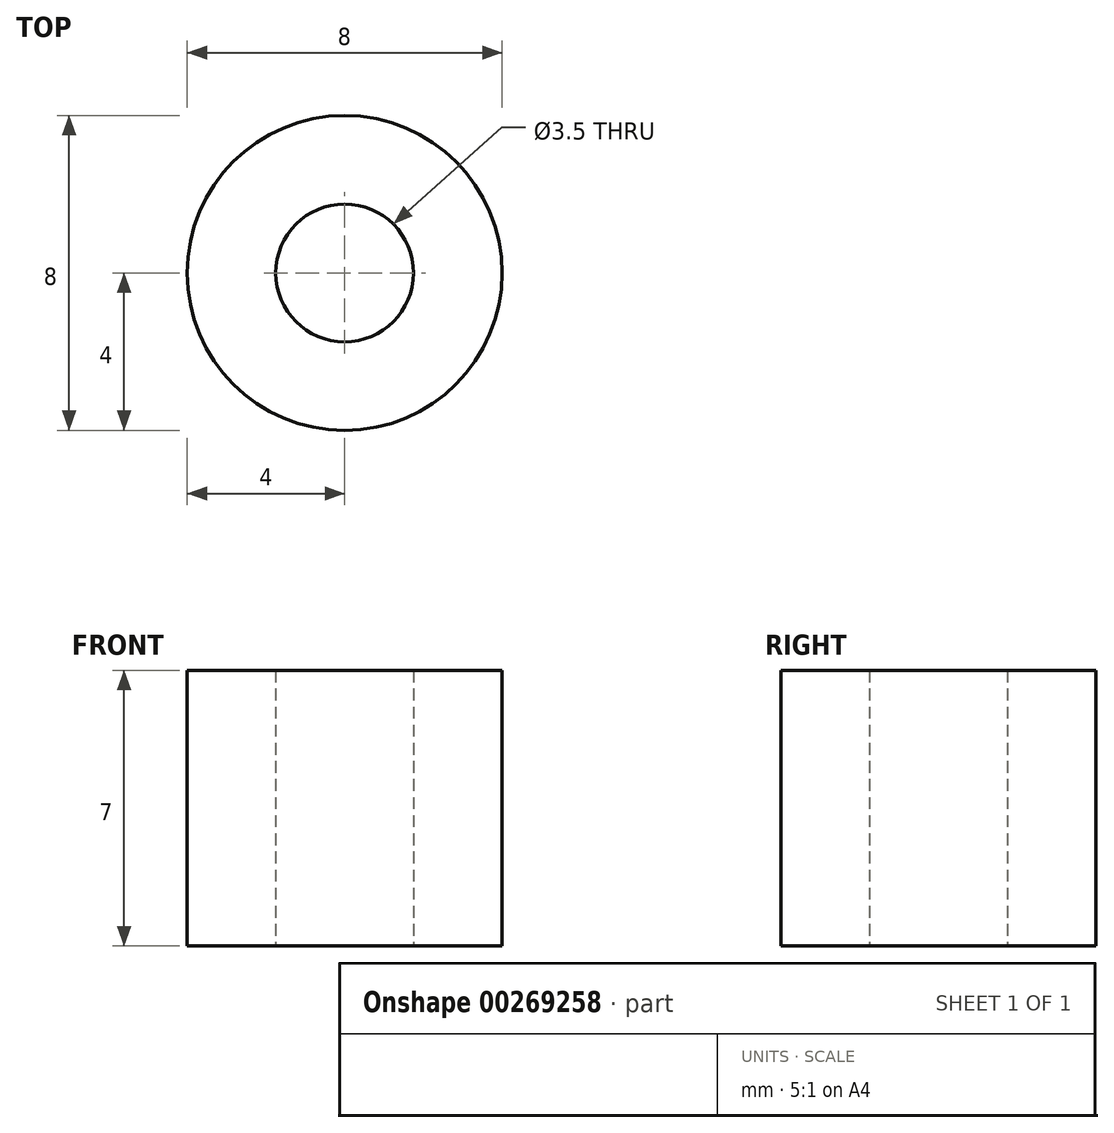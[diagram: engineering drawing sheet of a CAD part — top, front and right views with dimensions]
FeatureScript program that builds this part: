
annotation { "Feature Type Name" : "Feature", "Feature Type Description" : "" }
export const myFeature = defineFeature(function(context is Context, id is Id, definition is map)
    precondition{}
    {
        {
            var Q0;
            Q0=qCreatedBy(makeId("Top.planeOp"),FACE);
            var sketch = newSketch(context, id + "F0", { "sketchPlane" : qUnion([Q0])});
            skCircle(sketch, "E0", {"center": v(0, 0) * mm, "radius": 1.75 * mm});
            skCircle(sketch, "E1", {"center": v(0, 0) * mm, "radius": 4 * mm});
            skSolve(sketch);
        }
        {
            var Q0;
            Q0 = qSketchRegion(id + "F0", true);
            extrude(context, id + "F1", {"entities" : qUnion([Q0]), "depth" : 7 * mm});
        }
    });
